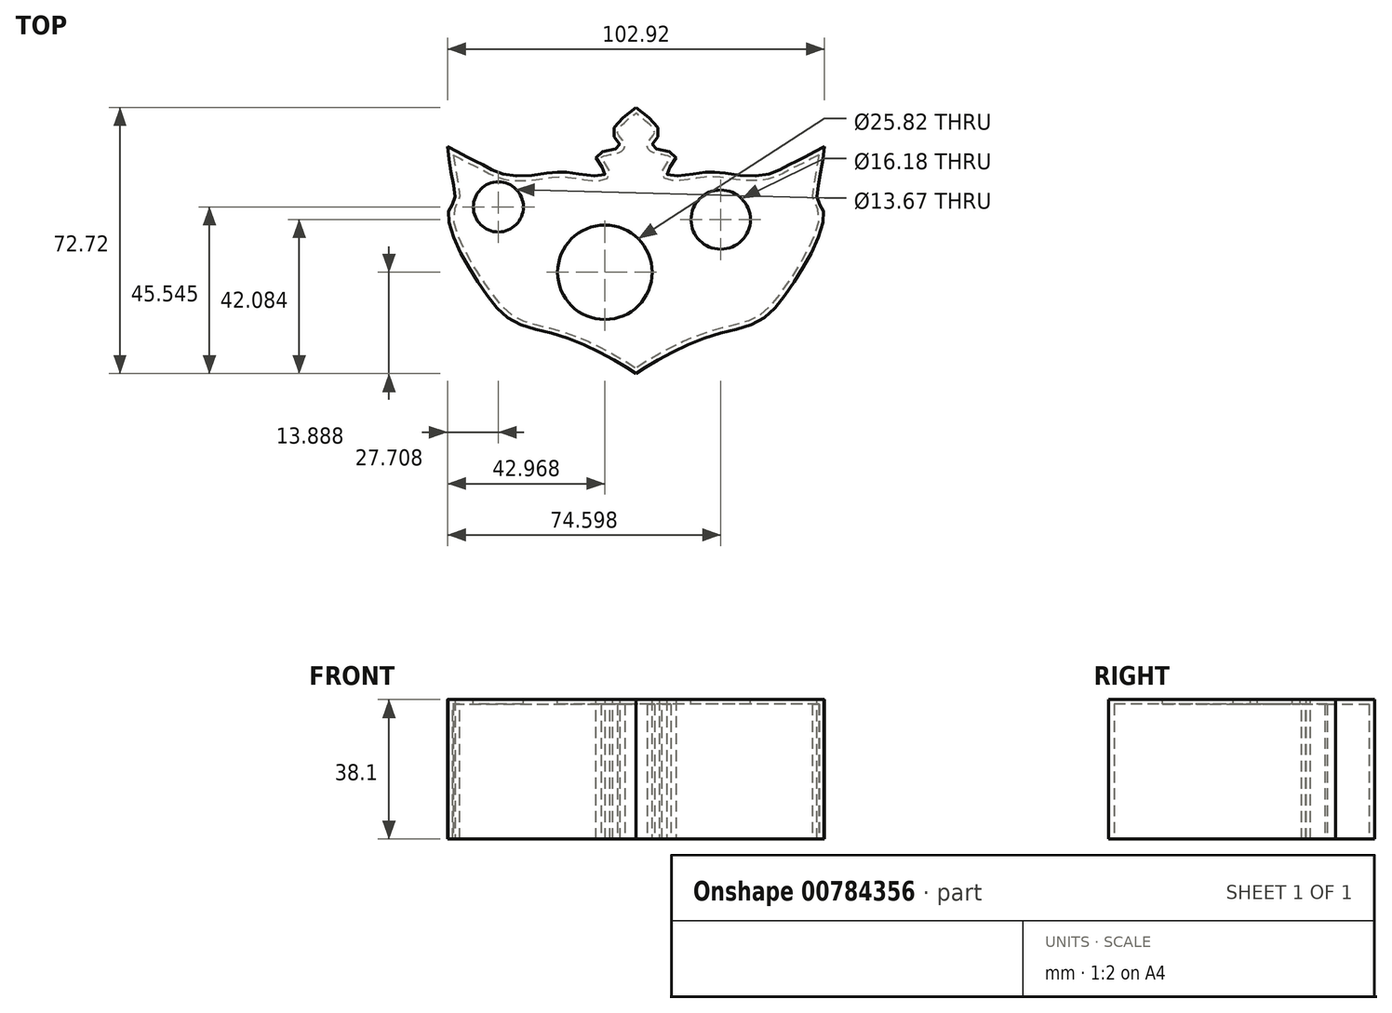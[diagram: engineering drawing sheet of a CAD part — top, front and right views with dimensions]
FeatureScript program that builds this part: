
annotation { "Feature Type Name" : "Feature", "Feature Type Description" : "" }
export const myFeature = defineFeature(function(context is Context, id is Id, definition is map)
    precondition{}
    {
        {
            var Q0;
            Q0=qCreatedBy(makeId("Top.planeOp"),FACE);
            var sketch = newSketch(context, id + "F0", { "sketchPlane" : qUnion([Q0])});
            skFitSpline(sketch, "E0", {"points": [v(-51.46, 26.72) * mm, v(-50.24, 18.48) * mm, v(-49.62, 11.76) * mm, v(-51.15, 9.31) * mm, v(-49.01, 0) * mm, v(-41.68, -12.37) * mm, v(-33.74, -20.92) * mm, v(-21.83, -24.58) * mm, v(-8.1, -30.39) * mm, v(0, -35.31) * mm], "startDerivative": vector(9.6, -76.33) * mm, "endDerivative": vector(44.23, -33.01) * mm});
            skFitSpline(sketch, "E1", {"points": [v(-51.46, 26.72) * mm, v(-45.65, 23.67) * mm, v(-41.38, 21.53) * mm, v(-34.36, 18.78) * mm, v(-22.45, 19.7) * mm, v(-16.95, 19.4) * mm, v(-8.4, 19.4) * mm, v(-10.84, 24.28) * mm, v(-4.43, 26.72) * mm, v(-6.26, 30.08) * mm, v(0, 37.4) * mm], "startDerivative": vector(62.25, -33.52) * mm, "endDerivative": vector(86.9, 64.92) * mm});
            skFitSpline(sketch, "E2.MirrorCS", {"points": [v(51.46, 26.72) * mm, v(45.65, 23.67) * mm, v(41.38, 21.53) * mm, v(34.36, 18.78) * mm, v(22.45, 19.7) * mm, v(16.95, 19.4) * mm, v(8.4, 19.4) * mm, v(10.84, 24.28) * mm, v(4.43, 26.72) * mm, v(6.26, 30.08) * mm, v(0, 37.4) * mm], "startDerivative": vector(-62.25, -33.52) * mm, "endDerivative": vector(-86.9, 64.92) * mm});
            skFitSpline(sketch, "E3.MirrorCS", {"points": [v(51.46, 26.72) * mm, v(50.24, 18.48) * mm, v(49.62, 11.76) * mm, v(51.15, 9.31) * mm, v(49.01, 0) * mm, v(41.68, -12.37) * mm, v(33.74, -20.92) * mm, v(21.83, -24.58) * mm, v(8.1, -30.39) * mm, v(0, -35.31) * mm], "startDerivative": vector(-9.6, -76.33) * mm, "endDerivative": vector(-44.23, -33.01) * mm});
            skSolve(sketch);
        }
        {
            var Q0;
            Q0 = qSketchRegion(id + "F0", true);
            extrude(context, id + "F1", {"entities" : qUnion([Q0]), "depth" : 38.1 * mm, "offsetDistance" : 25.4 * mm});
        }
        {
            var Q0;
            Q0=makeQuery(id+"F1.opExtrude","CAP_FACE",FACE,{"disambiguationData":[OSD([sQuery(id+"F0.wireOp",EDGE,"E0"),sQuery(id+"F0.wireOp",EDGE,"E1"),sQuery(id+"F0.wireOp",EDGE,"E2.MirrorCS"),sQuery(id+"F0.wireOp",EDGE,"E3.MirrorCS")])],"isStart":true});
            shell(context, id + "F2", {"entities" : qUnion([Q0]), "thickness" : 1.27 * mm});
        }
        {
            var Q0;
            Q0=makeQuery(id+"F1.opExtrude","CAP_FACE",FACE,{"disambiguationData":[OSD([sQuery(id+"F0.wireOp",EDGE,"E0"),sQuery(id+"F0.wireOp",EDGE,"E1"),sQuery(id+"F0.wireOp",EDGE,"E2.MirrorCS"),sQuery(id+"F0.wireOp",EDGE,"E3.MirrorCS")])],"isStart":false});
            var sketch = newSketch(context, id + "F3", { "sketchPlane" : qUnion([Q0])});
            skCircle(sketch, "E4", {"center": v(-37.57, 10.24) * mm, "radius": 6.83 * mm});
            skCircle(sketch, "E5", {"center": v(23.14, 6.77) * mm, "radius": 8.1 * mm});
            skCircle(sketch, "E6", {"center": v(-8.5, -7.6) * mm, "radius": 12.9 * mm});
            skSolve(sketch);
        }
        {
            var Q0;
            Q0 = qSketchRegion(id + "F3", true);
            extrude(context, id + "F4", {"entities" : qUnion([Q0]), "operationType" : NewBodyOperationType.REMOVE, "oppositeDirection" : true, "depth" : 25.4 * mm, "offsetDistance" : 25.4 * mm});
        }
    });
